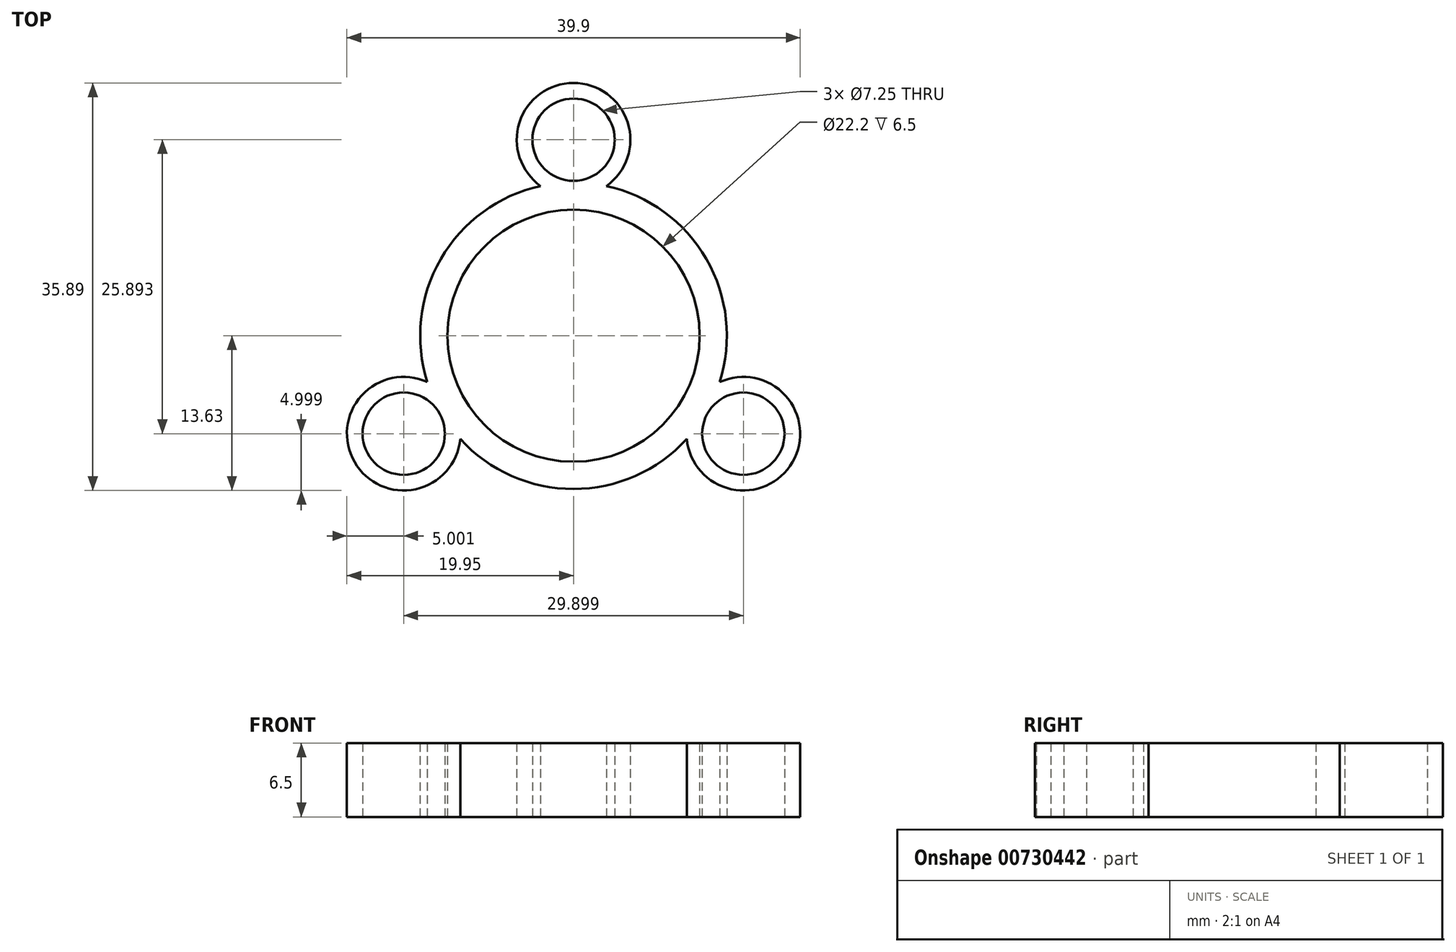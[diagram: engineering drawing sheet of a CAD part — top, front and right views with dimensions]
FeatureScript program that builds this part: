
annotation { "Feature Type Name" : "Feature", "Feature Type Description" : "" }
export const myFeature = defineFeature(function(context is Context, id is Id, definition is map)
    precondition{}
    {
        {
            var Q0;
            Q0=qCreatedBy(makeId("Top.planeOp"),FACE);
            var sketch = newSketch(context, id + "F0", { "sketchPlane" : qUnion([Q0])});
            skCircle(sketch, "E0", {"center": v(0, 0) * mm, "radius": 11.1 * mm});
            skCircle(sketch, "E1", {"center": v(0, 0) * mm, "radius": 13.5 * mm});
            skCircle(sketch, "E2", {"center": v(0, 17.26) * mm, "radius": 3.62 * mm});
            skCircle(sketch, "E3", {"center": v(0, 17.26) * mm, "radius": 5 * mm});
            skCircle(sketch, "E4.1.0", {"center": v(-14.95, -8.63) * mm, "radius": 3.62 * mm});
            skCircle(sketch, "E4.1.1", {"center": v(-14.95, -8.63) * mm, "radius": 5 * mm});
            skCircle(sketch, "E4.2.0", {"center": v(14.95, -8.63) * mm, "radius": 3.62 * mm});
            skCircle(sketch, "E4.2.1", {"center": v(14.95, -8.63) * mm, "radius": 5 * mm});
            skSolve(sketch);
        }
        {
            var Q0;
            Q0=makeQuery(id+"F0.imprint","IMPRINT",FACE,{"disambiguationData":[TD([[makeQuery(id+"F0.imprint","IMPRINT",EDGE,{"derivedFrom":sQuery(id+"F0.wireOp",EDGE,"E2")}),-1.0]])]});
            var Q1;
            Q1=makeQuery(id+"F0.imprint","IMPRINT",FACE,{"disambiguationData":[TD([[makeQuery(id+"F0.imprint","IMPRINT",EDGE,{"derivedFrom":sQuery(id+"F0.wireOp",EDGE,"E4.2.0")}),-1.0]])]});
            var Q2;
            Q2=makeQuery(id+"F0.imprint","IMPRINT",FACE,{"disambiguationData":[TD([[makeQuery(id+"F0.imprint","IMPRINT",EDGE,{"derivedFrom":sQuery(id+"F0.wireOp",EDGE,"E0")}),-1.0]])]});
            var Q3;
            Q3=makeQuery(id+"F0.imprint","IMPRINT",FACE,{"disambiguationData":[TD([[makeQuery(id+"F0.imprint","IMPRINT",EDGE,{"derivedFrom":sQuery(id+"F0.wireOp",EDGE,"E4.1.0")}),-1.0]])]});
            var Q4;
            {var subQ0=sQuery(id+"F0.wireOp",EDGE,"E4.2.1");var subQ1=sQuery(id+"F0.wireOp",EDGE,"E1");var subQ2=makeQuery(id+"F0.imprint","INTERSECT",VERTEX,{"disambiguationData":[OD(0.0)],"derivedFrom":[subQ1,subQ0]});Q4=makeQuery(id+"F0.imprint","IMPRINT",FACE,{"disambiguationData":[TD([[makeQuery(id+"F0.imprint","IMPRINT",EDGE,{"disambiguationData":[TD([[subQ2,-1.0]])],"derivedFrom":subQ1}),1.0]])]});}
            var Q5;
            {var subQ0=sQuery(id+"F0.wireOp",EDGE,"E3");var subQ1=sQuery(id+"F0.wireOp",EDGE,"E1");var subQ2=makeQuery(id+"F0.imprint","INTERSECT",VERTEX,{"disambiguationData":[OD(0.0)],"derivedFrom":[subQ1,subQ0]});Q5=makeQuery(id+"F0.imprint","IMPRINT",FACE,{"disambiguationData":[TD([[makeQuery(id+"F0.imprint","IMPRINT",EDGE,{"disambiguationData":[TD([[subQ2,1.0]])],"derivedFrom":subQ1}),1.0]])]});}
            var Q6;
            {var subQ0=sQuery(id+"F0.wireOp",EDGE,"E4.1.1");var subQ1=sQuery(id+"F0.wireOp",EDGE,"E1");var subQ2=makeQuery(id+"F0.imprint","INTERSECT",VERTEX,{"disambiguationData":[OD(0.0)],"derivedFrom":[subQ1,subQ0]});Q6=makeQuery(id+"F0.imprint","IMPRINT",FACE,{"disambiguationData":[TD([[makeQuery(id+"F0.imprint","IMPRINT",EDGE,{"disambiguationData":[TD([[subQ2,-1.0]])],"derivedFrom":subQ1}),1.0]])]});}
            extrude(context, id + "F1", {"entities" : qUnion([Q0, Q1, Q2, Q3, Q4, Q5, Q6]), "depth" : 6.5 * mm, "offsetDistance" : 25 * mm});
        }
    });
